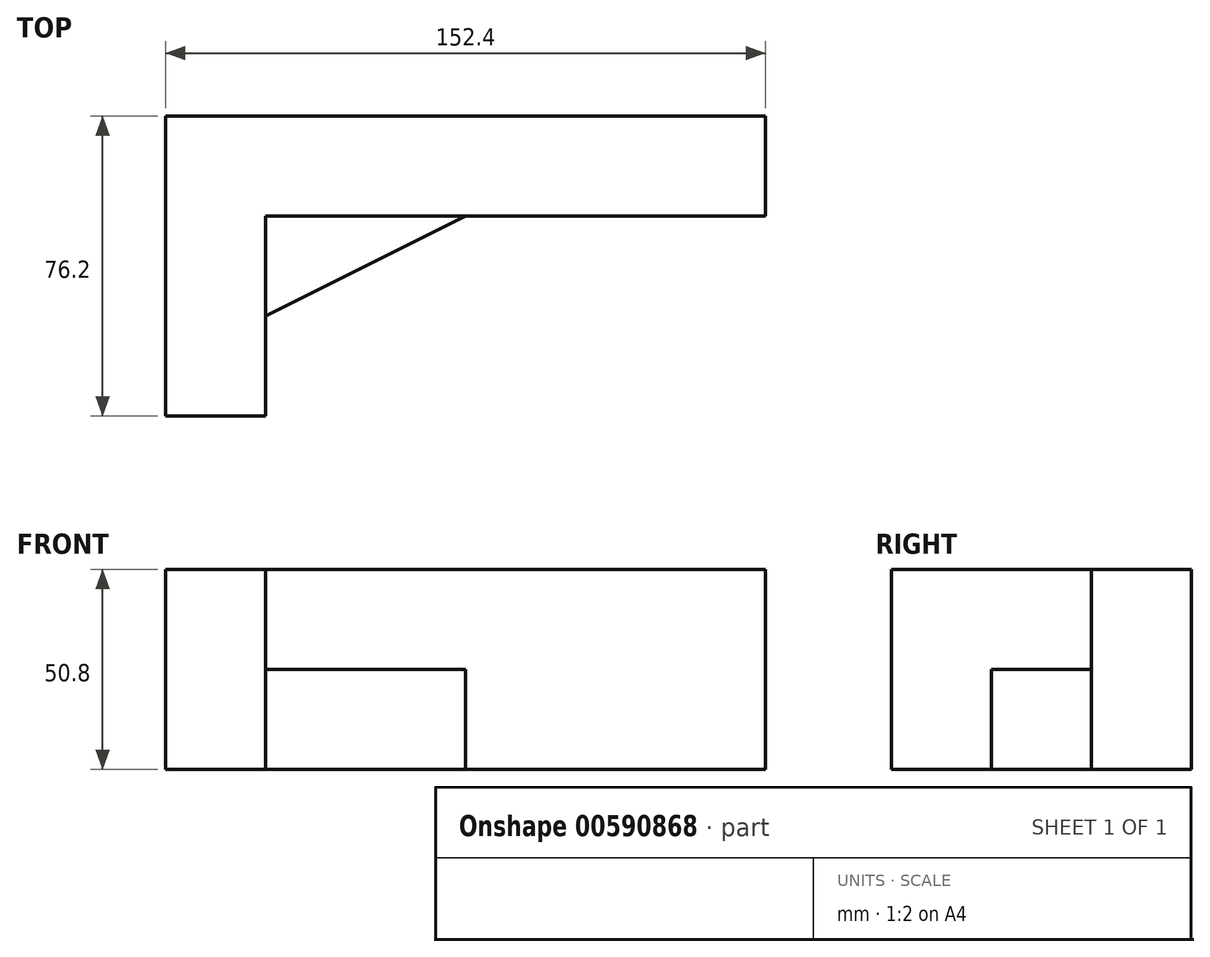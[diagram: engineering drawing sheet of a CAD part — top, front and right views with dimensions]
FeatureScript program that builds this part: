
annotation { "Feature Type Name" : "Feature", "Feature Type Description" : "" }
export const myFeature = defineFeature(function(context is Context, id is Id, definition is map)
    precondition{}
    {
        {
            var Q0;
            Q0=qCreatedBy(makeId("Front.planeOp"),FACE);
            var sketch = newSketch(context, id + "F0", { "sketchPlane" : qUnion([Q0])});
            skLineSegment(sketch, "E0.bottom", {"start": v(0, 0) * mm, "end": v(152.4, 0) * mm});
            skLineSegment(sketch, "E0.top", {"start": v(0, 50.8) * mm, "end": v(152.4, 50.8) * mm});
            skLineSegment(sketch, "E0.left", {"start": v(0, 0) * mm, "end": v(0, 50.8) * mm});
            skLineSegment(sketch, "E0.right", {"start": v(152.4, 0) * mm, "end": v(152.4, 50.8) * mm});
            skSolve(sketch);
        }
        {
            var Q0;
            Q0 = qSketchRegion(id + "F0", true);
            extrude(context, id + "F1", {"entities" : qUnion([Q0]), "oppositeDirection" : true, "depth" : 76.2 * mm, "offsetDistance" : 25.4 * mm});
        }
        {
            var Q0;
            Q0=makeQuery(id+"F1.opExtrude","SWEPT_FACE",FACE,{"disambiguationData":[OSD([sQuery(id+"F0.wireOp",EDGE,"E0.top")])]});
            var sketch = newSketch(context, id + "F2", { "sketchPlane" : qUnion([Q0])});
            skLineSegment(sketch, "E1", {"start": v(0, 0) * mm, "end": v(0, 76.2) * mm});
            skLineSegment(sketch, "E2", {"start": v(0, 76.2) * mm, "end": v(152.4, 76.2) * mm});
            skLineSegment(sketch, "E3", {"start": v(152.4, 76.2) * mm, "end": v(152.4, 50.8) * mm});
            skLineSegment(sketch, "E4", {"start": v(152.4, 50.8) * mm, "end": v(25.4, 50.8) * mm});
            skLineSegment(sketch, "E5", {"start": v(25.4, 50.8) * mm, "end": v(25.4, 0) * mm});
            skLineSegment(sketch, "E6", {"start": v(25.4, 0) * mm, "end": v(0, 0) * mm});
            skSolve(sketch);
        }
        {
            var Q0;
            {var subQ0=sQuery(id+"F2.wireOp",EDGE,"E4");Q0=makeQuery(id+"F2.imprint","IMPRINT",FACE,{"disambiguationData":[TD([[makeQuery(id+"F2.imprint","IMPRINT",EDGE,{"derivedFrom":subQ0}),1.0]])]});}
            extrude(context, id + "F3", {"entities" : qUnion([Q0]), "operationType" : NewBodyOperationType.REMOVE, "oppositeDirection" : true, "depth" : 25.4 * mm, "offsetDistance" : 25.4 * mm});
        }
        {
            var Q0;
            Q0=makeQuery(id+"F3.boolean.opBoolean","COPY",FACE,{"derivedFrom":makeQuery(id+"F3.opExtrude","CAP_FACE",FACE,{"disambiguationData":[OSD([sQuery(id+"F0.wireOp",EDGE,"E0.top"),sQuery(id+"F0.wireOp",EDGE,"E0.right"),sQuery(id+"F2.wireOp",EDGE,"E4"),sQuery(id+"F2.wireOp",EDGE,"E5")])],"isStart":false})});
            var sketch = newSketch(context, id + "F4", { "sketchPlane" : qUnion([Q0])});
            skLineSegment(sketch, "E7", {"start": v(25.4, 25.4) * mm, "end": v(76.2, 50.8) * mm});
            skLineSegment(sketch, "E8", {"start": v(76.2, 50.8) * mm, "end": v(25.4, 50.8) * mm});
            skLineSegment(sketch, "E9", {"start": v(25.4, 50.8) * mm, "end": v(25.4, 25.4) * mm});
            skSolve(sketch);
        }
        {
            var Q0;
            {var subQ3=sQuery(id+"F4.wireOp",EDGE,"E7");Q0=makeQuery(id+"F4.imprint","IMPRINT",FACE,{"disambiguationData":[TD([[makeQuery(id+"F4.imprint","IMPRINT",EDGE,{"derivedFrom":subQ3}),-1.0]])]});}
            extrude(context, id + "F5", {"entities" : qUnion([Q0]), "operationType" : NewBodyOperationType.REMOVE, "oppositeDirection" : true, "depth" : 25.4 * mm, "offsetDistance" : 25.4 * mm});
        }
    });
